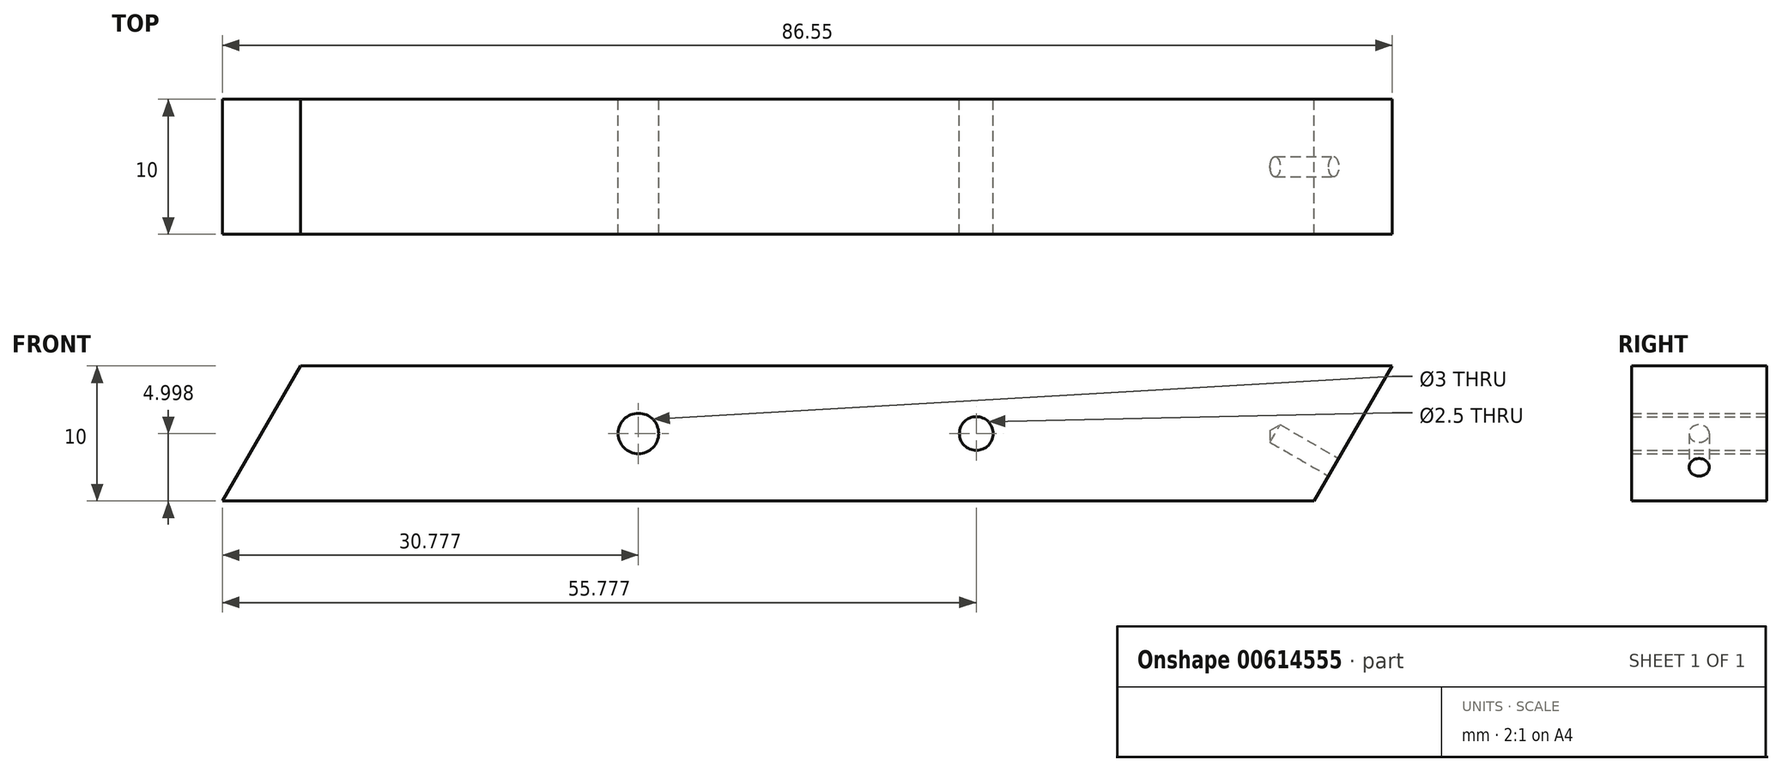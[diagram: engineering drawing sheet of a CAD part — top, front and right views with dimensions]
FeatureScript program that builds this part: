
annotation { "Feature Type Name" : "Feature", "Feature Type Description" : "" }
export const myFeature = defineFeature(function(context is Context, id is Id, definition is map)
    precondition{}
    {
        {
            var Q0;
            Q0=qCreatedBy(makeId("Front.planeOp"),FACE);
            var sketch = newSketch(context, id + "F0", { "sketchPlane" : qUnion([Q0])});
            skLineSegment(sketch, "E0.bottom", {"start": v(-39.28, -3.07) * mm, "end": v(35.72, -3.07) * mm});
            skLineSegment(sketch, "E0.top", {"start": v(-39.28, -13.07) * mm, "end": v(35.72, -13.07) * mm});
            skCircle(sketch, "E1", {"center": v(-14.28, -8.07) * mm, "radius": 1.5 * mm});
            skCircle(sketch, "E2", {"center": v(10.72, -8.07) * mm, "radius": 1.25 * mm});
            skLineSegment(sketch, "E3", {"start": v(35.72, -3.07) * mm, "end": v(41.5, -3.07) * mm});
            skLineSegment(sketch, "E4", {"start": v(35.72, -13.07) * mm, "end": v(41.5, -3.07) * mm});
            skLineSegment(sketch, "E5", {"start": v(-39.28, -3.07) * mm, "end": v(-45.06, -13.07) * mm});
            skLineSegment(sketch, "E6", {"start": v(-39.28, -13.07) * mm, "end": v(-45.06, -13.07) * mm});
            skSolve(sketch);
        }
        {
            var Q0;
            Q0 = qSketchRegion(id + "F0", true);
            extrude(context, id + "F1", {"entities" : qUnion([Q0]), "endBound" : BoundingType.SYMMETRIC, "depth" : 10 * mm, "offsetDistance" : 25 * mm});
        }
        {
            var Q0;
            Q0=makeQuery(id+"F1.opExtrude","SWEPT_FACE",FACE,{"disambiguationData":[OSD([sQuery(id+"F0.wireOp",EDGE,"E4")])]});
            var sketch = newSketch(context, id + "F2", { "sketchPlane" : qUnion([Q0])});
            skPoint(sketch, "E7", {"position": v(0, 9.42) * mm});
            skSolve(sketch);
        }
        {
            var Q0;
            Q0=sQuery(id+"F2.wireOp",VERTEX,"E7");
            var Q1;
            Q1=makeQuery(id+"F1.opExtrude","SWEPT_BODY",BODY,{"disambiguationData":[OSD([sQuery(id+"F0.wireOp",EDGE,"E0.bottom"),sQuery(id+"F0.wireOp",EDGE,"E0.top"),sQuery(id+"F0.wireOp",EDGE,"E1"),sQuery(id+"F0.wireOp",EDGE,"E2"),sQuery(id+"F0.wireOp",EDGE,"E3"),sQuery(id+"F0.wireOp",EDGE,"E4"),sQuery(id+"F0.wireOp",EDGE,"E5"),sQuery(id+"F0.wireOp",EDGE,"E6")])]});
            hole(context, id + "F3", {"style" : HoleStyle.SIMPLE, "endStyle" : HoleEndStyle.BLIND, "holeDiameter" : 1.5 * mm, "majorDiameter" : 5 * mm, "holeDepth" : 5 * mm, "isTappedThrough" : true, "tappedDepth" : 12 * mm, "tapClearance" : 3, "locations" : qUnion([Q0]), "scope" : qUnion([Q1])});
        }
    });
